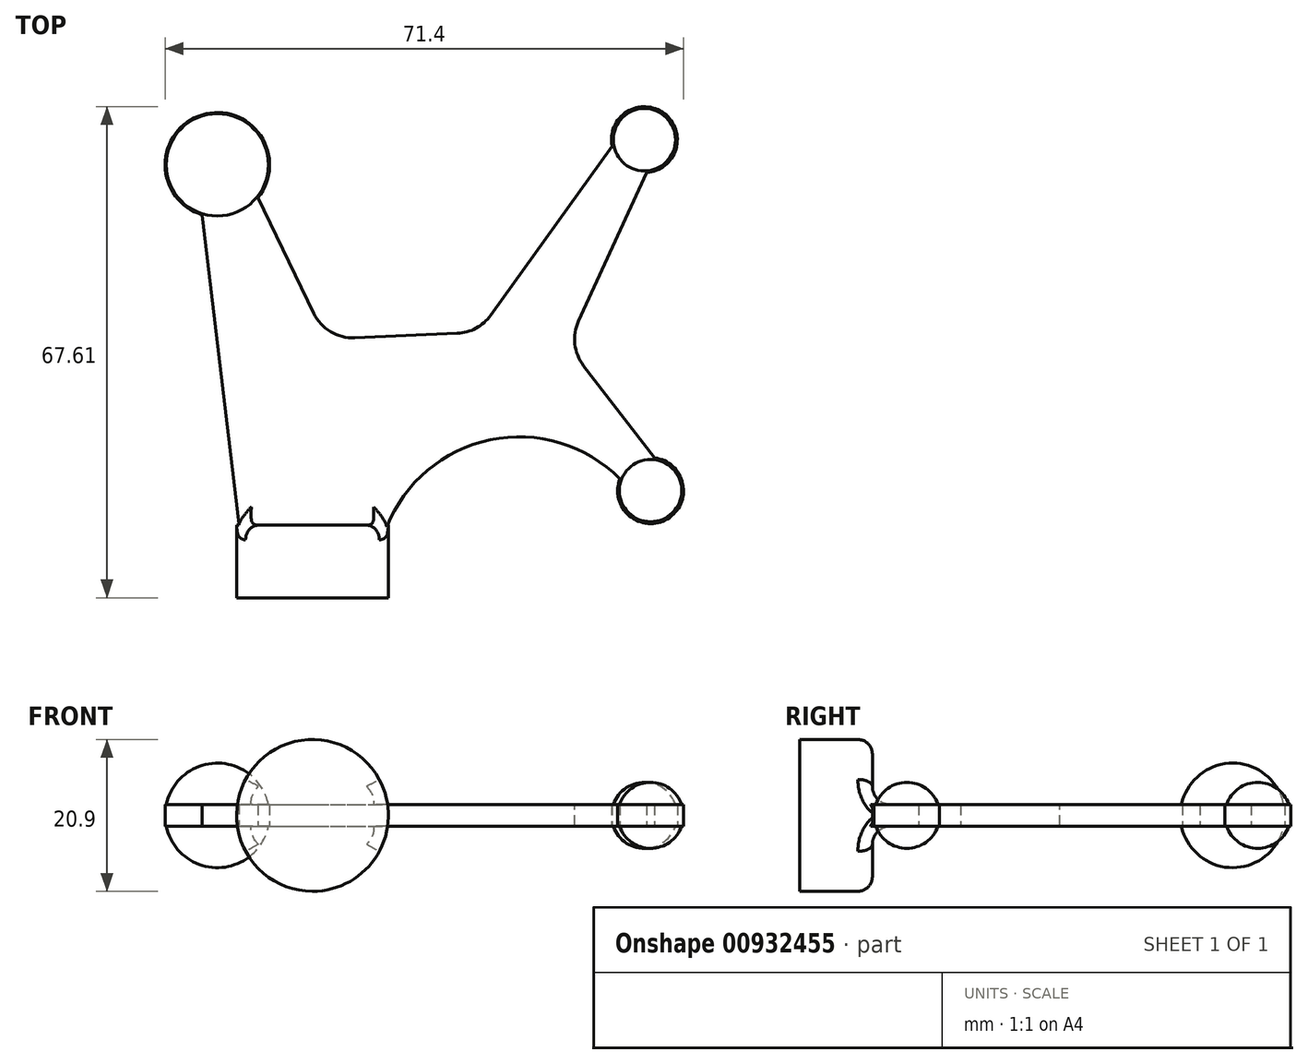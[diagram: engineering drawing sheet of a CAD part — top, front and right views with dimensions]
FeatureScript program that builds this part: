
annotation { "Feature Type Name" : "Feature", "Feature Type Description" : "" }
export const myFeature = defineFeature(function(context is Context, id is Id, definition is map)
    precondition{}
    {
        {
            var Q0;
            Q0=qCreatedBy(makeId("Top.planeOp"),FACE);
            var sketch = newSketch(context, id + "F0", { "sketchPlane" : qUnion([Q0])});
            skCircle(sketch, "E0", {"center": v(-13.1, 49.61) * mm, "radius": 7.2 * mm});
            skCircle(sketch, "E1", {"center": v(45.7, 53.07) * mm, "radius": 4.54 * mm});
            skCircle(sketch, "E2", {"center": v(46.56, 4.76) * mm, "radius": 4.54 * mm});
            skLineSegment(sketch, "E3", {"start": v(-13.1, 49.61) * mm, "end": v(0, 0) * mm, "construction": true});
            skLineSegment(sketch, "E4", {"start": v(0, 0) * mm, "end": v(45.7, 53.07) * mm, "construction": true});
            skLineSegment(sketch, "E5", {"start": v(46.56, 4.76) * mm, "end": v(19.47, 22.61) * mm, "construction": true});
            skLineSegment(sketch, "E6", {"start": v(-10.1, 0) * mm, "end": v(10.34, 0) * mm});
            skLineSegment(sketch, "E7", {"start": v(-10.1, 0) * mm, "end": v(-15.18, 42.72) * mm});
            skLineSegment(sketch, "E8", {"start": v(-7.5, 45.09) * mm, "end": v(1.88, 25.63) * mm});
            skLineSegment(sketch, "E9", {"start": v(1.88, 25.63) * mm, "end": v(22.85, 26.53) * mm});
            skLineSegment(sketch, "E10", {"start": v(22.85, 26.53) * mm, "end": v(41.25, 52.17) * mm});
            skLineSegment(sketch, "E11", {"start": v(46.03, 48.54) * mm, "end": v(35.13, 24.81) * mm});
            skLineSegment(sketch, "E12", {"start": v(35.13, 24.81) * mm, "end": v(47.1, 9.27) * mm});
            skArc(sketch, "E13", {"start": v(42.32, 6.4) * mm, "mid": v(24.61, 11.78) * mm, "end": v(10.34, 0) * mm});
            skSolve(sketch);
        }
        {
            var Q0;
            Q0 = qSketchRegion(id + "F0", true);
            extrude(context, id + "F1", {"entities" : qUnion([Q0]), "endBound" : BoundingType.SYMMETRIC, "depth" : 3 * mm, "offsetDistance" : 25 * mm});
        }
        {
            var Q0;
            Q0=qCreatedBy(makeId("Top.planeOp"),FACE);
            var sketch = newSketch(context, id + "F2", { "sketchPlane" : qUnion([Q0])});
            skArc(sketch, "E14.0", {"start": v(-13.1, 56.81) * mm, "mid": v(-20.3, 49.61) * mm, "end": v(-13.1, 42.42) * mm});
            skPoint(sketch, "E15.orphan", {"position": v(-15.18, 42.72) * mm});
            skArc(sketch, "E16.converted", {"start": v(45.7, 57.6) * mm, "mid": v(41.16, 53.07) * mm, "end": v(45.7, 48.53) * mm});
            skPoint(sketch, "E17.orphan", {"position": v(41.25, 52.17) * mm});
            skArc(sketch, "E18.converted", {"start": v(46.56, 9.3) * mm, "mid": v(42.02, 4.76) * mm, "end": v(46.56, 0.22) * mm});
            skLineSegment(sketch, "E19", {"start": v(-13.1, 42.42) * mm, "end": v(-13.1, 56.81) * mm});
            skLineSegment(sketch, "E20", {"start": v(45.7, 48.53) * mm, "end": v(45.7, 57.6) * mm});
            skLineSegment(sketch, "E21", {"start": v(46.56, 0.22) * mm, "end": v(46.56, 9.3) * mm});
            skPoint(sketch, "E22.orphan", {"position": v(-7.5, 45.09) * mm});
            skSolve(sketch);
        }
        {
            var Q0;
            Q0=makeQuery(id+"F2.imprint","IMPRINT",FACE,{"disambiguationData":[TD([[makeQuery(id+"F2.imprint","IMPRINT",EDGE,{"derivedFrom":sQuery(id+"F2.wireOp",EDGE,"E18.converted")}),1.0]])]});
            var Q1;
            Q1=sQuery(id+"F2.wireOp",EDGE,"E21");
            revolve(context, id + "F3", {"operationType" : NewBodyOperationType.ADD, "surfaceOperationType" : NewSurfaceOperationType.NEW, "entities" : qUnion([Q0]), "axis" : qUnion([Q1]), "revolveType" : RevolveType.FULL});
        }
        {
            var Q0;
            Q0=makeQuery(id+"F2.imprint","IMPRINT",FACE,{"disambiguationData":[TD([[makeQuery(id+"F2.imprint","IMPRINT",EDGE,{"derivedFrom":sQuery(id+"F2.wireOp",EDGE,"E16.converted")}),1.0]])]});
            var Q1;
            Q1=sQuery(id+"F2.wireOp",EDGE,"E20");
            revolve(context, id + "F4", {"operationType" : NewBodyOperationType.ADD, "surfaceOperationType" : NewSurfaceOperationType.NEW, "entities" : qUnion([Q0]), "axis" : qUnion([Q1]), "revolveType" : RevolveType.FULL});
        }
        {
            var Q0;
            Q0=makeQuery(id+"F2.imprint","IMPRINT",FACE,{"disambiguationData":[TD([[makeQuery(id+"F2.imprint","IMPRINT",EDGE,{"derivedFrom":sQuery(id+"F2.wireOp",EDGE,"E14.0")}),1.0]])]});
            var Q1;
            Q1=sQuery(id+"F2.wireOp",EDGE,"E19");
            revolve(context, id + "F5", {"operationType" : NewBodyOperationType.ADD, "surfaceOperationType" : NewSurfaceOperationType.NEW, "entities" : qUnion([Q0]), "axis" : qUnion([Q1]), "revolveType" : RevolveType.FULL});
        }
        {
            var Q0;
            Q0=makeQuery(id+"F1.opExtrude","SWEPT_FACE",FACE,{"disambiguationData":[OSD([sQuery(id+"F0.wireOp",EDGE,"E6")])]});
            var sketch = newSketch(context, id + "F6", { "sketchPlane" : qUnion([Q0])});
            skCircle(sketch, "E23", {"center": v(0, 0) * mm, "radius": 10.45 * mm});
            skSolve(sketch);
        }
        {
            var Q0;
            Q0 = qSketchRegion(id + "F6", true);
            extrude(context, id + "F7", {"entities" : qUnion([Q0]), "operationType" : NewBodyOperationType.ADD, "depth" : 10 * mm, "offsetDistance" : 25 * mm});
        }
        {
            var Q0;
            Q0=makeQuery(id+"F1.opExtrude","CAP_EDGE",EDGE,{"disambiguationData":[OSD([sQuery(id+"F0.wireOp",EDGE,"E6")])],"isStart":false});
            var Q1;
            Q1=makeQuery(id+"F1.opExtrude","CAP_EDGE",EDGE,{"disambiguationData":[OSD([sQuery(id+"F0.wireOp",EDGE,"E6")])],"isStart":true});
            fillet(context, id + "F8", {"entities" : qUnion([Q0, Q1]), "radius" : 2.5 * mm, "tangentPropagation" : true, "allowEdgeOverflow" : false});
        }
        {
            var Q0;
            {var subQ0=sQuery(id+"F0.wireOp",EDGE,"E13");var subQ1=sQuery(id+"F0.wireOp",EDGE,"E12");var subQ2=sQuery(id+"F0.wireOp",EDGE,"E11");var subQ3=sQuery(id+"F0.wireOp",EDGE,"E10");var subQ4=sQuery(id+"F0.wireOp",EDGE,"E9");var subQ5=sQuery(id+"F0.wireOp",EDGE,"E8");var subQ6=sQuery(id+"F0.wireOp",EDGE,"E7");var subQ7=sQuery(id+"F0.wireOp",EDGE,"E6");var subQ8=sQuery(id+"F0.wireOp",EDGE,"E2");var subQ9=sQuery(id+"F0.wireOp",EDGE,"E1");var subQ10=sQuery(id+"F0.wireOp",EDGE,"E0");var subQ11=sQuery(id+"F6.wireOp",EDGE,"E23");var subQ12=makeQuery(id+"F7.opExtrude","CAP_FACE",FACE,{"disambiguationData":[OSD([subQ11])],"isStart":true});Q0=makeQuery(id+"F8.opFillet","SPLIT",FACE,{"disambiguationData":[OD(0.0)],"derivedFrom":makeQuery(id+"F7.boolean.opBoolean","SPLIT",FACE,{"disambiguationData":[TD([makeQuery(id+"F1.opExtrude","CAP_FACE",FACE,{"disambiguationData":[OSD([subQ10,subQ9,subQ8,subQ7,subQ6,subQ5,subQ4,subQ3,subQ2,subQ1,subQ0])],"isStart":true}),makeQuery(id+"F1.opExtrude","CAP_FACE",FACE,{"disambiguationData":[OSD([subQ10,subQ9,subQ8,subQ7,subQ6,subQ5,subQ4,subQ3,subQ2,subQ1,subQ0])],"isStart":false}),makeQuery(id+"F1.opExtrude","SWEPT_FACE",FACE,{"disambiguationData":[OSD([subQ6])]}),makeQuery(id+"F1.opExtrude","SWEPT_FACE",FACE,{"disambiguationData":[OSD([subQ0])]}),makeQuery(id+"F7.opExtrude","SWEPT_FACE",FACE,{"disambiguationData":[OSD([subQ11])]}),subQ12])],"derivedFrom":subQ12})});}
            var Q1;
            {var subQ0=sQuery(id+"F0.wireOp",EDGE,"E13");var subQ1=sQuery(id+"F0.wireOp",EDGE,"E12");var subQ2=sQuery(id+"F0.wireOp",EDGE,"E11");var subQ3=sQuery(id+"F0.wireOp",EDGE,"E10");var subQ4=sQuery(id+"F0.wireOp",EDGE,"E9");var subQ5=sQuery(id+"F0.wireOp",EDGE,"E8");var subQ6=sQuery(id+"F0.wireOp",EDGE,"E7");var subQ7=sQuery(id+"F0.wireOp",EDGE,"E6");var subQ8=sQuery(id+"F0.wireOp",EDGE,"E2");var subQ9=sQuery(id+"F0.wireOp",EDGE,"E1");var subQ10=sQuery(id+"F0.wireOp",EDGE,"E0");var subQ11=sQuery(id+"F6.wireOp",EDGE,"E23");var subQ12=makeQuery(id+"F7.opExtrude","CAP_FACE",FACE,{"disambiguationData":[OSD([subQ11])],"isStart":true});Q1=makeQuery(id+"F8.opFillet","SPLIT",FACE,{"disambiguationData":[OD(1.0)],"derivedFrom":makeQuery(id+"F7.boolean.opBoolean","SPLIT",FACE,{"disambiguationData":[TD([makeQuery(id+"F1.opExtrude","CAP_FACE",FACE,{"disambiguationData":[OSD([subQ10,subQ9,subQ8,subQ7,subQ6,subQ5,subQ4,subQ3,subQ2,subQ1,subQ0])],"isStart":true}),makeQuery(id+"F1.opExtrude","CAP_FACE",FACE,{"disambiguationData":[OSD([subQ10,subQ9,subQ8,subQ7,subQ6,subQ5,subQ4,subQ3,subQ2,subQ1,subQ0])],"isStart":false}),makeQuery(id+"F1.opExtrude","SWEPT_FACE",FACE,{"disambiguationData":[OSD([subQ6])]}),makeQuery(id+"F1.opExtrude","SWEPT_FACE",FACE,{"disambiguationData":[OSD([subQ0])]}),makeQuery(id+"F7.opExtrude","SWEPT_FACE",FACE,{"disambiguationData":[OSD([subQ11])]}),subQ12])],"derivedFrom":subQ12})});}
            fillet(context, id + "F9", {"entities" : qUnion([Q0, Q1]), "radius" : 2 * mm, "tangentPropagation" : true, "allowEdgeOverflow" : false});
        }
        {
            var Q0;
            Q0=makeQuery(id+"F1.opExtrude","SWEPT_EDGE",EDGE,{"disambiguationData":[OSD([sQuery(id+"F0.wireOp",EDGE,"E9"),sQuery(id+"F0.wireOp",EDGE,"E10")])]});
            var Q1;
            Q1=makeQuery(id+"F1.opExtrude","SWEPT_EDGE",EDGE,{"disambiguationData":[OSD([sQuery(id+"F0.wireOp",EDGE,"E8"),sQuery(id+"F0.wireOp",EDGE,"E9")])]});
            var Q2;
            Q2=makeQuery(id+"F1.opExtrude","SWEPT_EDGE",EDGE,{"disambiguationData":[OSD([sQuery(id+"F0.wireOp",EDGE,"E11"),sQuery(id+"F0.wireOp",EDGE,"E12")])]});
            fillet(context, id + "F10", {"entities" : qUnion([Q0, Q1, Q2]), "radius" : 6 * mm, "tangentPropagation" : true, "allowEdgeOverflow" : false});
        }
    });
